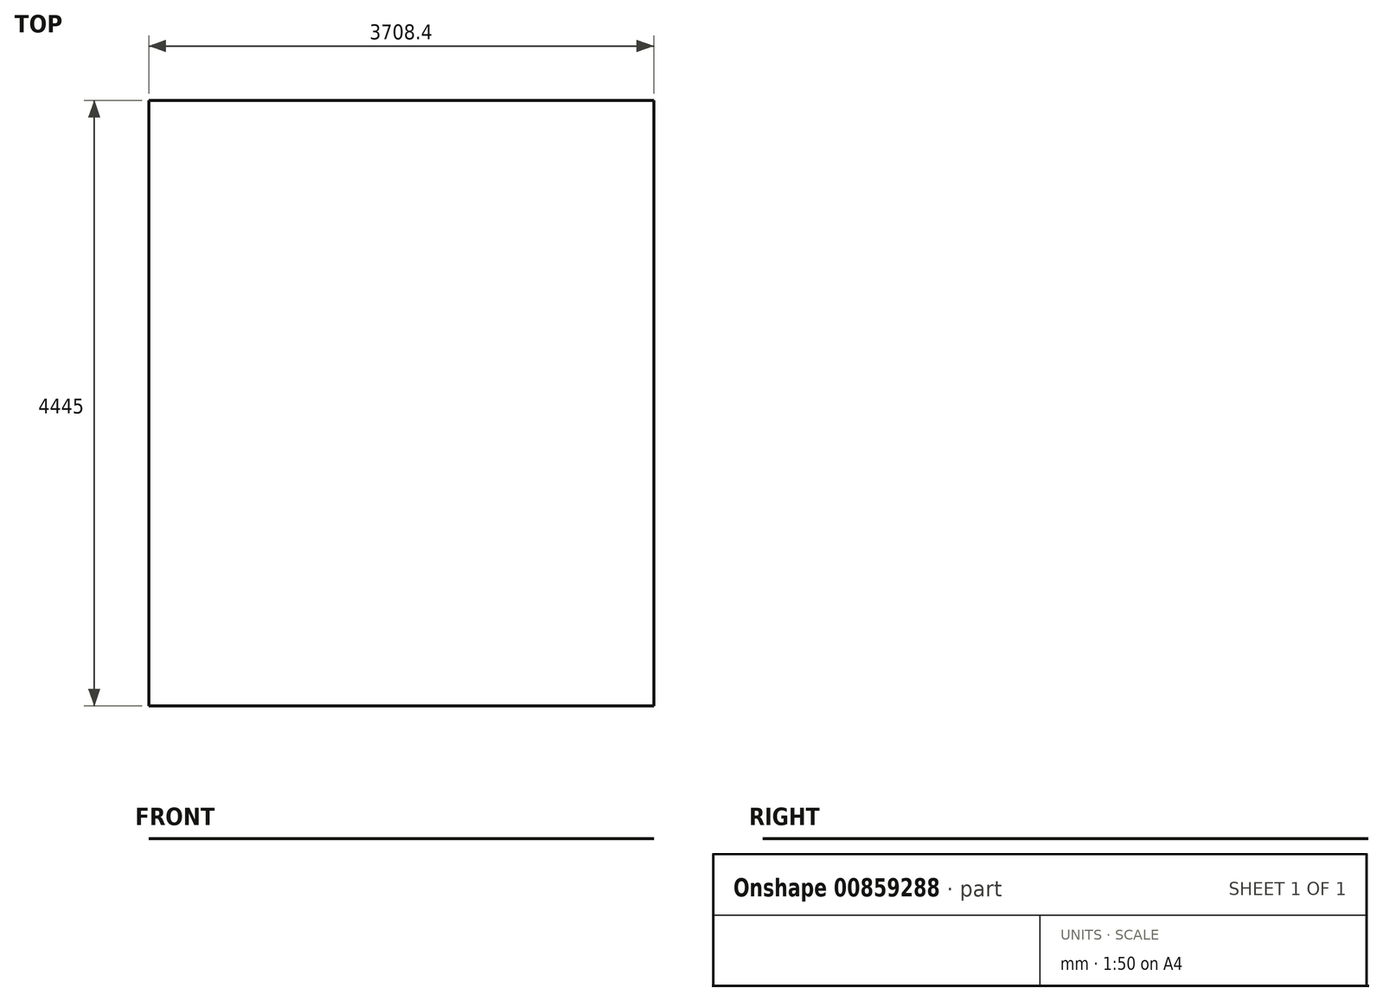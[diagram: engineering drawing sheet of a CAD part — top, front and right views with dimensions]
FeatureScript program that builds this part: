
annotation { "Feature Type Name" : "Feature", "Feature Type Description" : "" }
export const myFeature = defineFeature(function(context is Context, id is Id, definition is map)
    precondition{}
    {
        {
            var Q0;
            Q0=qCreatedBy(makeId("Top.planeOp"),FACE);
            var sketch = newSketch(context, id + "F0", { "sketchPlane" : qUnion([Q0])});
            skLineSegment(sketch, "E0.bottom", {"start": v(0, 0) * mm, "end": v(3708.4, 0) * mm});
            skLineSegment(sketch, "E0.top", {"start": v(0, 4445) * mm, "end": v(3708.4, 4445) * mm});
            skLineSegment(sketch, "E0.left", {"start": v(0, 0) * mm, "end": v(0, 4445) * mm});
            skLineSegment(sketch, "E0.right", {"start": v(3708.4, 0) * mm, "end": v(3708.4, 4445) * mm});
            skSolve(sketch);
        }
        {
            var Q0;
            Q0=makeQuery(id+"F0.imprint","IMPRINT",FACE,{"disambiguationData":[TD([[makeQuery(id+"F0.imprint","IMPRINT",EDGE,{"derivedFrom":sQuery(id+"F0.wireOp",EDGE,"E0.bottom")}),1.0]])]});
            extrude(context, id + "F1", {"entities" : qUnion([Q0]), "depth" : 1 / 406.4 * mm, "offsetDistance" : 25.4 * mm});
        }
    });
